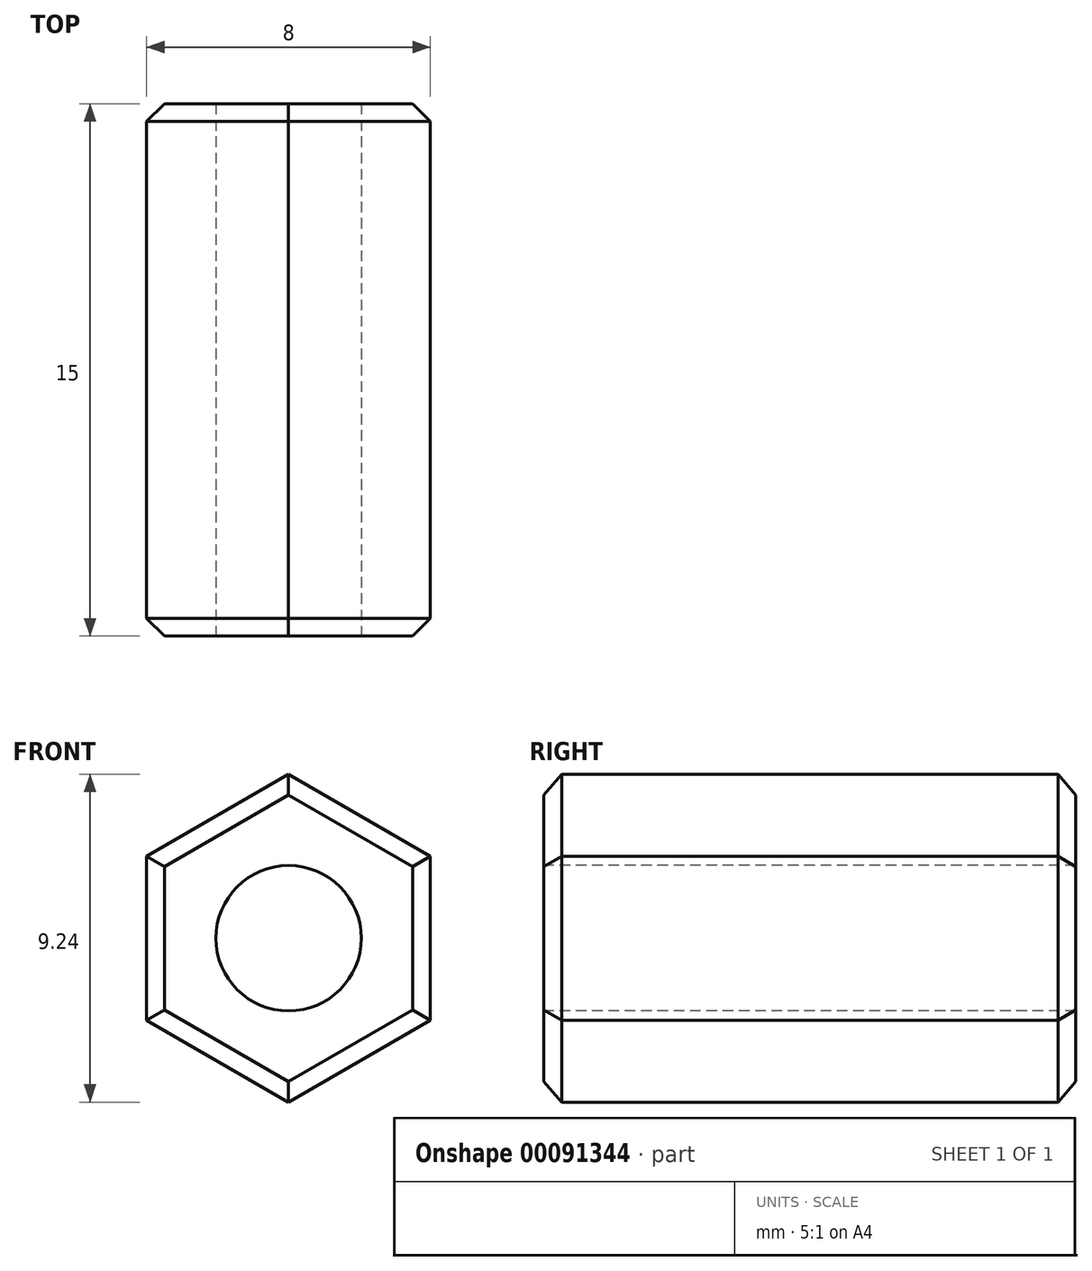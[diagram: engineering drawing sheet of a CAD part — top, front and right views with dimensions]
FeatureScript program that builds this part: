
annotation { "Feature Type Name" : "Feature", "Feature Type Description" : "" }
export const myFeature = defineFeature(function(context is Context, id is Id, definition is map)
    precondition{}
    {
        {
            var Q0;
            Q0=qCreatedBy(makeId("Front.planeOp"),FACE);
            var sketch = newSketch(context, id + "F0", { "sketchPlane" : qUnion([Q0])});
            skCircle(sketch, "E0.cCircle", {"center": v(0, 0) * mm, "radius": 4 * mm, "construction": true});
            skLineSegment(sketch, "E0.0", {"start": v(4, 2.3) * mm, "end": v(4, -2.3) * mm});
            skLineSegment(sketch, "E0.1", {"start": v(4, -2.3) * mm, "end": v(0, -4.62) * mm});
            skLineSegment(sketch, "E0.2", {"start": v(0, -4.62) * mm, "end": v(-4, -2.3) * mm});
            skLineSegment(sketch, "E0.3", {"start": v(-4, -2.3) * mm, "end": v(-4, 2.3) * mm});
            skLineSegment(sketch, "E0.4", {"start": v(-4, 2.3) * mm, "end": v(0, 4.62) * mm});
            skLineSegment(sketch, "E0.5", {"start": v(0, 4.62) * mm, "end": v(4, 2.3) * mm});
            skPoint(sketch, "E0.0.midPoint", {"position": v(4, 0) * mm});
            skSolve(sketch);
        }
        {
            var Q0;
            Q0=makeQuery(id+"F0.imprint","IMPRINT",FACE,{"disambiguationData":[TD([[makeQuery(id+"F0.imprint","IMPRINT",EDGE,{"derivedFrom":sQuery(id+"F0.wireOp",EDGE,"E0.0")}),-1.0]])]});
            extrude(context, id + "F1", {"entities" : qUnion([Q0]), "depth" : 15 * mm});
        }
        {
            var Q0;
            Q0=sQuery(id+"F0.wireOp",VERTEX,"E0.cCircle.center");
            var Q1;
            Q1=makeQuery(id+"F1.opExtrude","SWEPT_BODY",BODY,{"disambiguationData":[OSD([sQuery(id+"F0.wireOp",EDGE,"E0.0"),sQuery(id+"F0.wireOp",EDGE,"E0.1"),sQuery(id+"F0.wireOp",EDGE,"E0.2"),sQuery(id+"F0.wireOp",EDGE,"E0.3"),sQuery(id+"F0.wireOp",EDGE,"E0.4"),sQuery(id+"F0.wireOp",EDGE,"E0.5")])]});
            hole(context, id + "F2", {"style" : HoleStyle.SIMPLE, "endStyle" : HoleEndStyle.THROUGH, "oppositeDirection" : true, "standardTappedOrClearance" : lookupTablePath({ "standard" : "ISO", "engagement" : "75%", "pitch" : "0.9 mm", "size" : "M5", "type" : "Tapped" }), "standardBlindInLast" : lookupTablePath({ "standard" : "ISO", "engagement" : "75%", "pitch" : "0.9 mm", "size" : "M5", "type" : "Tapped" }), "holeDiameter" : 4.1 * mm, "locations" : qUnion([Q0]), "scope" : qUnion([Q1]), "isTappedThrough" : true, "showTappedDepth" : true, "startStyle" : HoleStartStyle.SKETCH});
        }
        {
            var Q0;
            Q0=makeQuery(id+"F1.opExtrude","CAP_EDGE",EDGE,{"disambiguationData":[OSD([sQuery(id+"F0.wireOp",EDGE,"E0.2")])],"isStart":true});
            var Q1;
            Q1=makeQuery(id+"F1.opExtrude","CAP_EDGE",EDGE,{"disambiguationData":[OSD([sQuery(id+"F0.wireOp",EDGE,"E0.3")])],"isStart":true});
            var Q2;
            Q2=makeQuery(id+"F1.opExtrude","CAP_EDGE",EDGE,{"disambiguationData":[OSD([sQuery(id+"F0.wireOp",EDGE,"E0.4")])],"isStart":true});
            var Q3;
            Q3=makeQuery(id+"F1.opExtrude","CAP_EDGE",EDGE,{"disambiguationData":[OSD([sQuery(id+"F0.wireOp",EDGE,"E0.5")])],"isStart":true});
            var Q4;
            Q4=makeQuery(id+"F1.opExtrude","CAP_EDGE",EDGE,{"disambiguationData":[OSD([sQuery(id+"F0.wireOp",EDGE,"E0.0")])],"isStart":true});
            var Q5;
            Q5=makeQuery(id+"F1.opExtrude","CAP_EDGE",EDGE,{"disambiguationData":[OSD([sQuery(id+"F0.wireOp",EDGE,"E0.1")])],"isStart":true});
            var Q6;
            Q6=makeQuery(id+"F1.opExtrude","CAP_EDGE",EDGE,{"disambiguationData":[OSD([sQuery(id+"F0.wireOp",EDGE,"E0.0")])],"isStart":false});
            var Q7;
            Q7=makeQuery(id+"F1.opExtrude","CAP_EDGE",EDGE,{"disambiguationData":[OSD([sQuery(id+"F0.wireOp",EDGE,"E0.5")])],"isStart":false});
            var Q8;
            Q8=makeQuery(id+"F1.opExtrude","CAP_EDGE",EDGE,{"disambiguationData":[OSD([sQuery(id+"F0.wireOp",EDGE,"E0.4")])],"isStart":false});
            var Q9;
            Q9=makeQuery(id+"F1.opExtrude","CAP_EDGE",EDGE,{"disambiguationData":[OSD([sQuery(id+"F0.wireOp",EDGE,"E0.3")])],"isStart":false});
            var Q10;
            Q10=makeQuery(id+"F1.opExtrude","CAP_EDGE",EDGE,{"disambiguationData":[OSD([sQuery(id+"F0.wireOp",EDGE,"E0.2")])],"isStart":false});
            var Q11;
            Q11=makeQuery(id+"F1.opExtrude","CAP_EDGE",EDGE,{"disambiguationData":[OSD([sQuery(id+"F0.wireOp",EDGE,"E0.1")])],"isStart":false});
            chamfer(context, id + "F3", {"entities" : qUnion([Q0, Q1, Q2, Q3, Q4, Q5, Q6, Q7, Q8, Q9, Q10, Q11]), "width" : .5 * mm, "tangentPropagation" : true});
        }
    });
